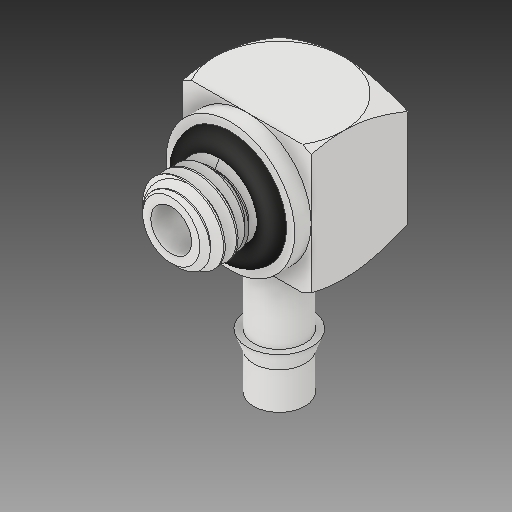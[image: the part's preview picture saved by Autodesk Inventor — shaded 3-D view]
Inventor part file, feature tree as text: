
AUTODESK INVENTOR PART (.ipt)
format: ipt  version: 2019.4 (Build 234330000, 330)  size: 437,248 bytes
history: native  units: in
note: dims shown in document units (in); Inventor stores cm internally (conversion verified against a paired STEP export)
features: revolve x1, other x1
ambient origin geometry x8: Origin, YZ Plane, XZ Plane, XY Plane, X Axis, Y Axis, Z Axis, Center Point
bodies: Solid1 (feature_tree), Solid2 (feature_tree)
feature tree (2):
  revolve  "REVOLVE2"  [1 undecoded]
  other  "CUT-EXTRUDE11"
note: 1 required parameter value undecoded (feature->parameter linkage not recoverable at this tier; creation-order binding heuristic only, values carry confidence <= 0.55)
